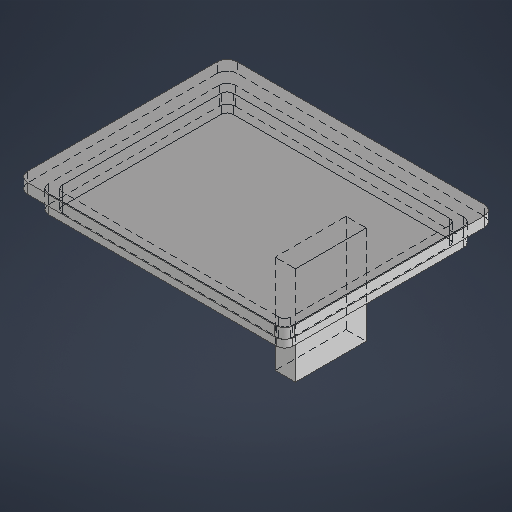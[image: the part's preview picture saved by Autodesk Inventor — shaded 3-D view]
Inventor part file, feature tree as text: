
AUTODESK INVENTOR PART (.ipt)
format: ipt  version: 2025.2 (Build 292293000, 293)  size: 214,528 bytes
history: native  units: mm
features: extrude x3, fillet x3, sketch x1
ambient origin geometry x8: Origin, YZ Plane, XZ Plane, XY Plane, X Axis, Y Axis, Z Axis, Center Point
bodies: Solid1 (feature_tree)
feature tree (7):
  sketch  "Sketch1"  dims[d0=5.0mm d1=0.0mm d2=9.0mm d3=0.0mm d4=48.5mm d5=0.0mm d6=5.0mm d7=4.0mm d8=3.0mm d9=0.5mm d10=4.0mm d11=10.0mm d12=35.0mm d13=24.0mm]
  extrude  "Extrusion1"  Depth=9.0mm TaperAngle=0.0deg
  extrude  "Extrusion2"  Depth=48.5mm TaperAngle=0.0deg
  extrude  "Extrusion3"  Depth=5.0mm
  fillet  "Fillet1"  Radius=4.0mm
  fillet  "Fillet2"  Radius=3.0mm
  fillet  "Fillet3"  Radius=0.5mm
